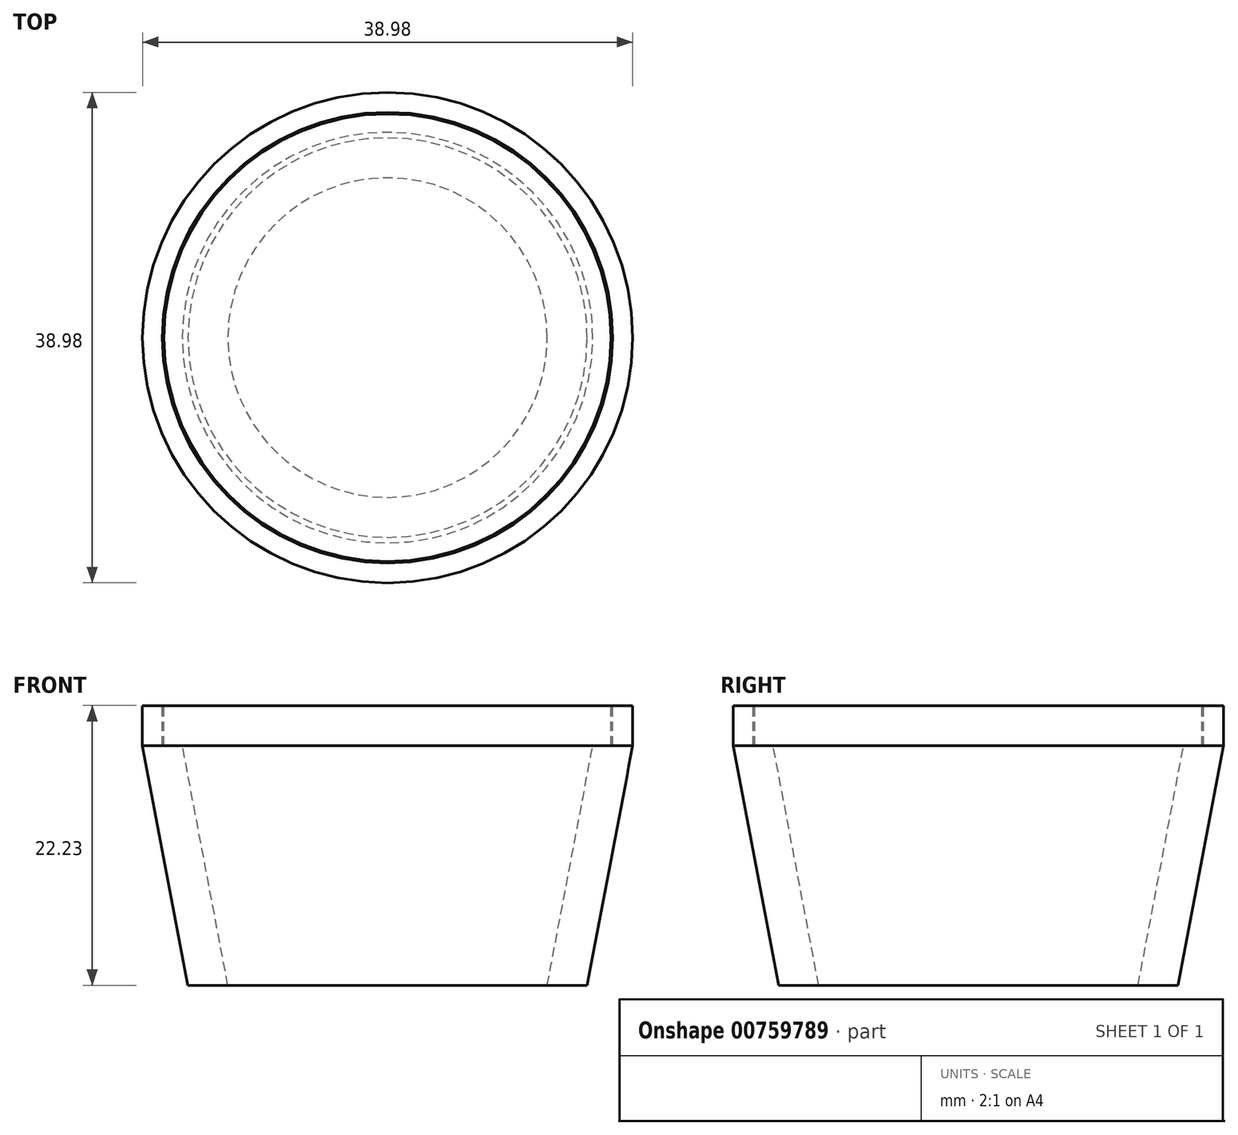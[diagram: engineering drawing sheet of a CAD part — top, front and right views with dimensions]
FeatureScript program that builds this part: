
annotation { "Feature Type Name" : "Feature", "Feature Type Description" : "" }
export const myFeature = defineFeature(function(context is Context, id is Id, definition is map)
    precondition{}
    {
        {
            var Q0;
            Q0=qCreatedBy(makeId("Front.planeOp"),FACE);
            var sketch = newSketch(context, id + "F0", { "sketchPlane" : qUnion([Q0])});
            skLineSegment(sketch, "E0", {"start": v(12.7, 0) * mm, "end": v(16.32, 19.05) * mm});
            skLineSegment(sketch, "E1", {"start": v(16.32, 19.05) * mm, "end": v(17.9, 19.05) * mm});
            skLineSegment(sketch, "E2", {"start": v(17.9, 19.05) * mm, "end": v(17.9, 22.23) * mm});
            skLineSegment(sketch, "E3", {"start": v(17.9, 22.23) * mm, "end": v(19.5, 22.23) * mm});
            skLineSegment(sketch, "E4", {"start": v(19.5, 22.23) * mm, "end": v(19.5, 19.05) * mm});
            skLineSegment(sketch, "E5", {"start": v(19.5, 19.05) * mm, "end": v(15.88, 0) * mm});
            skLineSegment(sketch, "E6", {"start": v(15.88, 0) * mm, "end": v(12.7, 0) * mm});
            skLineSegment(sketch, "E7", {"start": v(0, 43.4) * mm, "end": v(0, 0) * mm, "construction": true});
            skSolve(sketch);
        }
        {
            var Q0;
            Q0 = qSketchRegion(id + "F0", true);
            var Q1;
            Q1=sQuery(id+"F0.wireOp",EDGE,"E7");
            revolve(context, id + "F1", {"surfaceOperationType" : NewSurfaceOperationType.NEW, "entities" : qUnion([Q0]), "axis" : qUnion([Q1]), "revolveType" : RevolveType.FULL});
        }
        {
            var Q0;
            Q0=makeQuery(id+"F1.opRevolve","SWEPT_FACE",FACE,{"disambiguationData":[OSD([sQuery(id+"F0.wireOp",EDGE,"E3")])]});
            var sketch = newSketch(context, id + "F2", { "sketchPlane" : qUnion([Q0])});
            skCircle(sketch, "E8", {"center": v(0, 0) * mm, "radius": 17.78 * mm});
            skSolve(sketch);
        }
        {
            var Q0;
            Q0 = qSketchRegion(id + "F2", true);
            var Q1;
            Q1=makeQuery(id+"F1.opRevolve","SWEPT_FACE",FACE,{"disambiguationData":[OSD([sQuery(id+"F0.wireOp",EDGE,"E1")])]});
            extrude(context, id + "F3", {"entities" : qUnion([Q0]), "endBound" : BoundingType.UP_TO_SURFACE, "oppositeDirection" : true, "depth" : 25.4 * mm, "endBoundEntityFace" : qUnion([Q1]), "offsetDistance" : 25.4 * mm});
        }
    });
